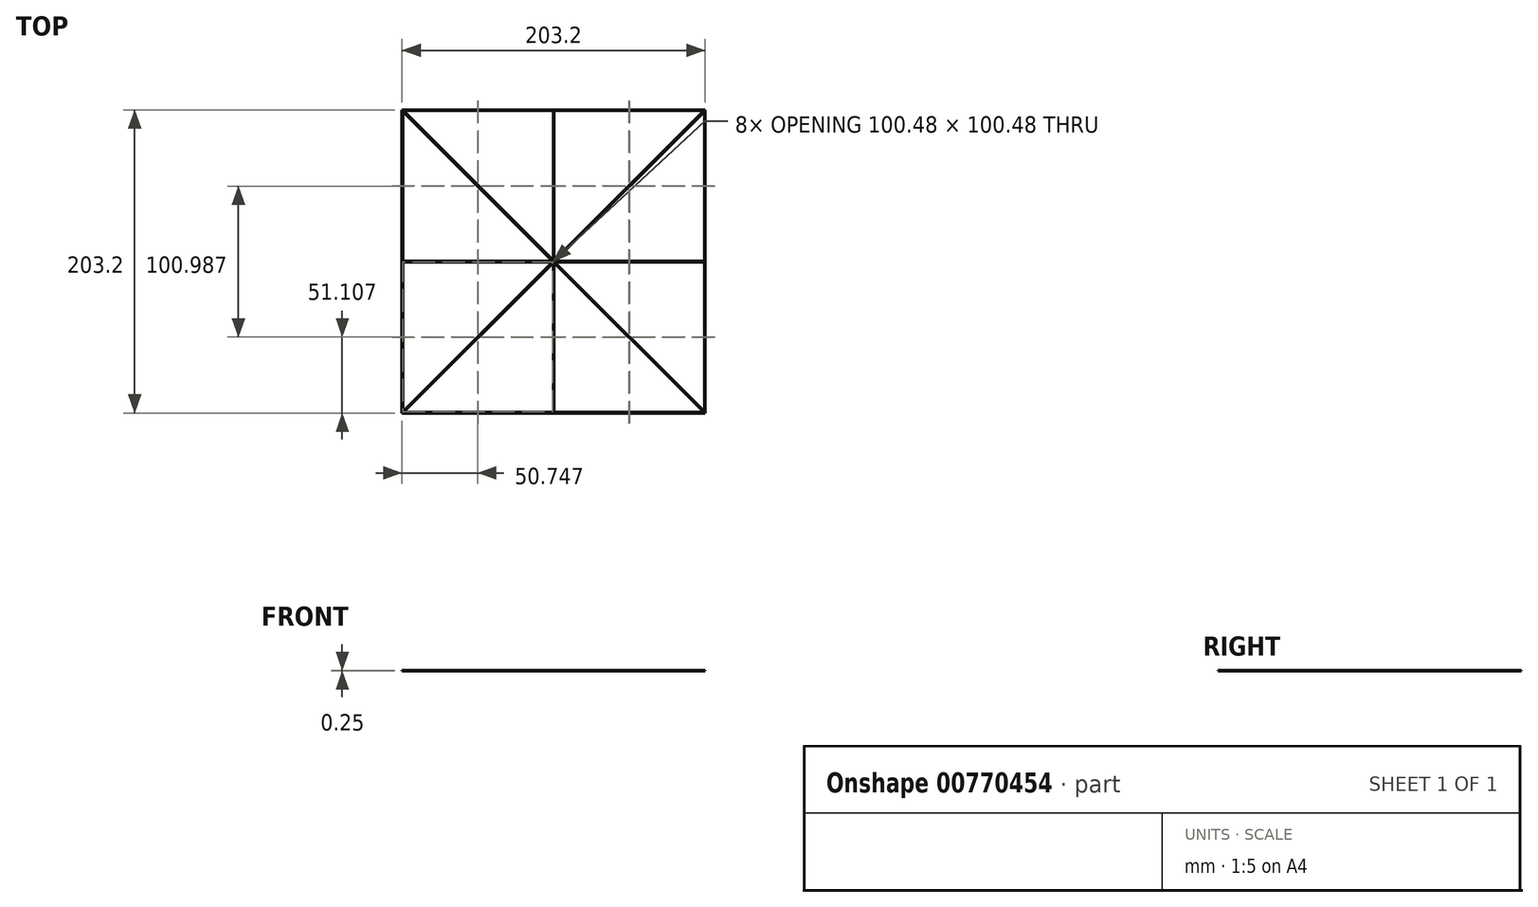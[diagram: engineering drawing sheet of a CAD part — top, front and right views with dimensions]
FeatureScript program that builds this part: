
annotation { "Feature Type Name" : "Feature", "Feature Type Description" : "" }
export const myFeature = defineFeature(function(context is Context, id is Id, definition is map)
    precondition{}
    {
        {
            var Q0;
            Q0=qCreatedBy(makeId("Top.planeOp"),FACE);
            var sketch = newSketch(context, id + "F0", { "sketchPlane" : qUnion([Q0])});
            skLineSegment(sketch, "E0.bottom", {"start": v(-101.6, -101.6) * mm, "end": v(101.6, -101.6) * mm, "construction": true});
            skLineSegment(sketch, "E0.top", {"start": v(-101.6, 101.6) * mm, "end": v(101.6, 101.6) * mm, "construction": true});
            skLineSegment(sketch, "E0.left", {"start": v(-101.6, -101.6) * mm, "end": v(-101.6, 101.6) * mm, "construction": true});
            skLineSegment(sketch, "E0.right", {"start": v(101.6, -101.6) * mm, "end": v(101.6, 101.6) * mm, "construction": true});
            skPoint(sketch, "E0.middle", {"position": v(0, 0) * mm});
            skLineSegment(sketch, "E1.bottom", {"start": v(-101.1, -101.1) * mm, "end": v(101.1, -101.1) * mm, "construction": true});
            skLineSegment(sketch, "E1.top", {"start": v(-101.1, 101.1) * mm, "end": v(101.1, 101.1) * mm, "construction": true});
            skLineSegment(sketch, "E1.left", {"start": v(-101.1, -101.1) * mm, "end": v(-101.1, 101.1) * mm, "construction": true});
            skLineSegment(sketch, "E1.right", {"start": v(101.1, -101.1) * mm, "end": v(101.1, 101.1) * mm, "construction": true});
            skLineSegment(sketch, "E2", {"start": v(0, 0) * mm, "end": v(0, 101.1) * mm, "construction": true});
            skLineSegment(sketch, "E3", {"start": v(-101.1, 101.1) * mm, "end": v(101.1, -101.1) * mm, "construction": true});
            skLineSegment(sketch, "E4", {"start": v(-101.1, -101.1) * mm, "end": v(101.1, 101.1) * mm, "construction": true});
            skLineSegment(sketch, "E5", {"start": v(0, 0) * mm, "end": v(-101.1, 0) * mm, "construction": true});
            skLineSegment(sketch, "E6", {"start": v(-0.25, 101.1) * mm, "end": v(-0.25, -101.1) * mm, "construction": true});
            skLineSegment(sketch, "E7", {"start": v(0.25, 101.1) * mm, "end": v(0.25, -101.1) * mm, "construction": true});
            skLineSegment(sketch, "E8", {"start": v(100.73, 101.1) * mm, "end": v(-101.1, -100.73) * mm, "construction": true});
            skLineSegment(sketch, "E9.0", {"start": v(101.1, 100.73) * mm, "end": v(-100.73, -101.1) * mm, "construction": true});
            skLineSegment(sketch, "E10.0", {"start": v(-101.1, 100.73) * mm, "end": v(100.73, -101.1) * mm, "construction": true});
            skLineSegment(sketch, "E11.0", {"start": v(-100.73, 101.1) * mm, "end": v(101.1, -100.73) * mm, "construction": true});
            skLineSegment(sketch, "E12.0", {"start": v(101.1, 0.25) * mm, "end": v(-101.1, 0.25) * mm, "construction": true});
            skLineSegment(sketch, "E13.0", {"start": v(101.1, -0.25) * mm, "end": v(-101.1, -0.25) * mm, "construction": true});
            skSolve(sketch);
        }
        {
            var Q0;
            Q0=qCreatedBy(makeId("Top.planeOp"),FACE);
            var sketch = newSketch(context, id + "F1", { "sketchPlane" : qUnion([Q0])});
            skPoint(sketch, "E14.middle", {"position": v(0, 0) * mm});
            skLineSegment(sketch, "E15.0", {"start": v(-101.6, 101.6) * mm, "end": v(101.6, 101.6) * mm});
            skLineSegment(sketch, "E16.1", {"start": v(101.6, -101.6) * mm, "end": v(101.6, 101.6) * mm});
            skLineSegment(sketch, "E17.1", {"start": v(-101.6, -101.6) * mm, "end": v(101.6, -101.6) * mm});
            skLineSegment(sketch, "E18.0", {"start": v(-101.6, -101.6) * mm, "end": v(-101.6, 101.6) * mm});
            skLineSegment(sketch, "E19.0", {"start": v(-100.73, 101.1) * mm, "end": v(-0.25, 101.1) * mm});
            skLineSegment(sketch, "E20.0", {"start": v(-0.25, 101.1) * mm, "end": v(-0.25, 0.61) * mm});
            skLineSegment(sketch, "E21.0", {"start": v(0.25, 101.1) * mm, "end": v(0.25, 0.61) * mm});
            skLineSegment(sketch, "E22.0", {"start": v(-101.1, -100.73) * mm, "end": v(-101.1, -0.25) * mm});
            skLineSegment(sketch, "E23.0", {"start": v(-100.73, 101.1) * mm, "end": v(-0.25, 0.61) * mm});
            skLineSegment(sketch, "E24.0", {"start": v(-101.1, 100.73) * mm, "end": v(-0.61, 0.25) * mm});
            skLineSegment(sketch, "E25.0", {"start": v(101.1, -100.73) * mm, "end": v(101.1, -0.25) * mm});
            skLineSegment(sketch, "E26.0", {"start": v(-100.73, -101.1) * mm, "end": v(-0.25, -101.1) * mm});
            skLineSegment(sketch, "E27.0", {"start": v(101.1, 100.73) * mm, "end": v(0.61, 0.25) * mm});
            skLineSegment(sketch, "E28.0", {"start": v(100.73, 101.1) * mm, "end": v(0.25, 0.61) * mm});
            skLineSegment(sketch, "E29.0", {"start": v(101.1, 0.25) * mm, "end": v(0.61, 0.25) * mm});
            skLineSegment(sketch, "E30.0", {"start": v(101.1, -0.25) * mm, "end": v(0.61, -0.25) * mm});
            skLineSegment(sketch, "E31.trimOffspring", {"start": v(0.25, 101.1) * mm, "end": v(100.73, 101.1) * mm});
            skLineSegment(sketch, "E32.trimOffspring", {"start": v(0.25, -101.1) * mm, "end": v(100.73, -101.1) * mm});
            skLineSegment(sketch, "E33.trimOffspring", {"start": v(101.1, 0.25) * mm, "end": v(101.1, 100.73) * mm});
            skLineSegment(sketch, "E34.trimOffspring", {"start": v(-101.1, 0.25) * mm, "end": v(-101.1, 100.73) * mm});
            skLineSegment(sketch, "E35.trimOffspring", {"start": v(-0.61, 0.25) * mm, "end": v(-101.1, 0.25) * mm});
            skLineSegment(sketch, "E36.trimOffspring", {"start": v(0.61, -0.25) * mm, "end": v(101.1, -100.73) * mm});
            skLineSegment(sketch, "E37.trimOffspring", {"start": v(0.25, -0.61) * mm, "end": v(0.25, -101.1) * mm});
            skLineSegment(sketch, "E38.trimOffspring", {"start": v(0.25, -0.61) * mm, "end": v(100.73, -101.1) * mm});
            skLineSegment(sketch, "E39.trimOffspring", {"start": v(-0.25, -0.61) * mm, "end": v(-100.73, -101.1) * mm});
            skLineSegment(sketch, "E40.trimOffspring", {"start": v(-0.61, -0.25) * mm, "end": v(-101.1, -100.73) * mm});
            skLineSegment(sketch, "E41.trimOffspring", {"start": v(-0.61, -0.25) * mm, "end": v(-101.1, -0.25) * mm});
            skLineSegment(sketch, "E42.trimOffspring", {"start": v(-0.25, -0.61) * mm, "end": v(-0.25, -101.1) * mm});
            skPoint(sketch, "E43.orphan", {"position": v(-101.1, 101.1) * mm});
            skPoint(sketch, "E44.orphan", {"position": v(101.1, 101.1) * mm});
            skPoint(sketch, "E45.orphan", {"position": v(101.1, -101.1) * mm});
            skPoint(sketch, "E46.orphan", {"position": v(-101.1, -101.1) * mm});
            skSolve(sketch);
        }
        {
            var Q0;
            Q0=qSketchRegion(id+"F1",true);
            extrude(context, id + "F2", {"entities" : qUnion([Q0]), "depth" : 0.25 * mm, "offsetDistance" : 25.4 * mm});
        }
    });
